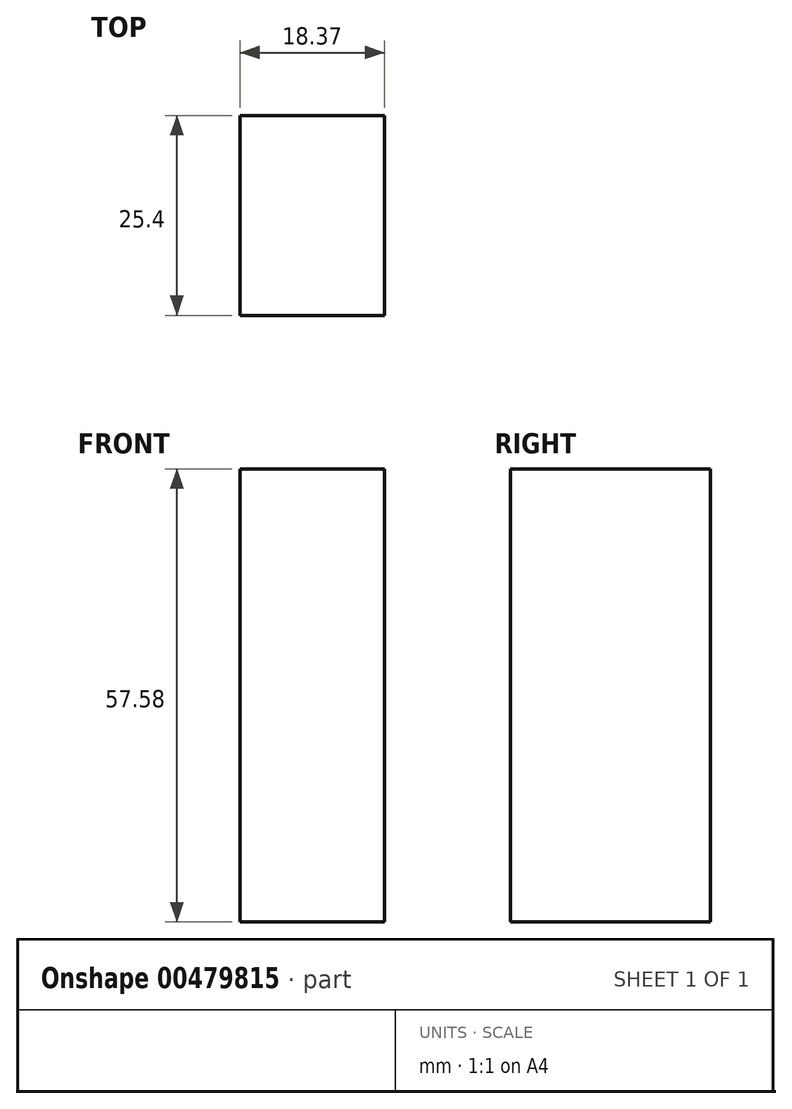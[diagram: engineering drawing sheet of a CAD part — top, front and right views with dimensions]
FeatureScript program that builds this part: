
annotation { "Feature Type Name" : "Feature", "Feature Type Description" : "" }
export const myFeature = defineFeature(function(context is Context, id is Id, definition is map)
    precondition{}
    {
        {
            var Q0;
            Q0=qCreatedBy(makeId("Front.planeOp"),FACE);
            var sketch = newSketch(context, id + "F0", { "sketchPlane" : qUnion([Q0])});
            skLineSegment(sketch, "E0.bottom", {"start": v(18.37, 0) * mm, "end": v(0, 0) * mm});
            skLineSegment(sketch, "E0.top", {"start": v(18.37, 57.58) * mm, "end": v(0, 57.58) * mm});
            skLineSegment(sketch, "E0.left", {"start": v(18.37, 0) * mm, "end": v(18.37, 57.58) * mm});
            skLineSegment(sketch, "E0.right", {"start": v(0, 0) * mm, "end": v(0, 57.58) * mm});
            skSolve(sketch);
        }
        {
            var Q0;
            Q0 = qSketchRegion(id + "F0", true);
            extrude(context, id + "F1", {"entities" : qUnion([Q0]), "depth" : 25.4 * mm});
        }
    });
